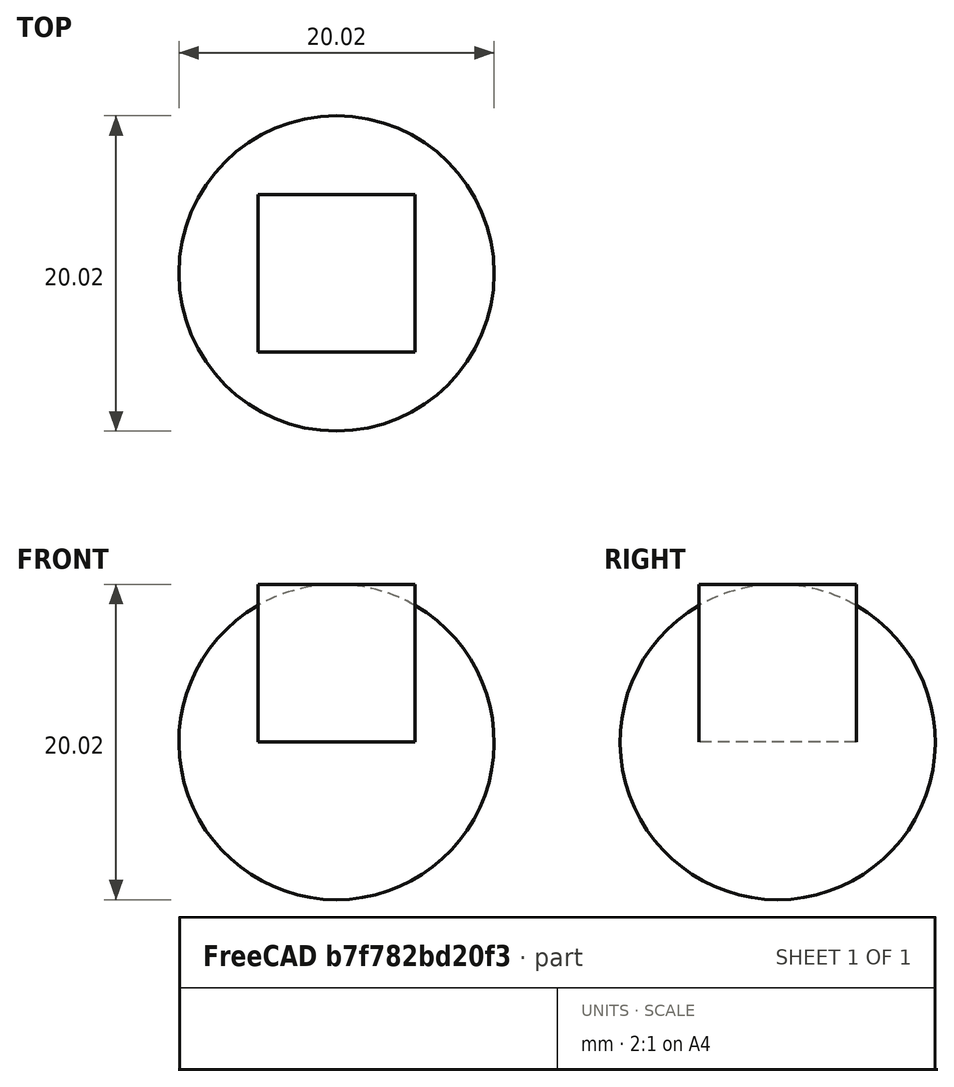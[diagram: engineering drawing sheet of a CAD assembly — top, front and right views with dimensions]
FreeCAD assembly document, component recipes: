
FREECAD ASSEMBLY — COMPONENT RECIPES ("test")

This assembly document has 2 components, labeled P0..P1 below (a component is one placed body or linked part). 2 of them carry a construction recipe — the FreeCAD feature program that regenerates the part from scratch, quoted from this document or its linked companion documents; the rest are supplied as boundary geometry only. No exploded tour is included for this assembly.
COMPONENT P0 — recipe-attached ("Cube", modeled in this document).
Construction recipe (the document's own serialized feature program — sketch geometry with constraints, then the solid features built on it; lengths are millimeters unless a unit is written):

FEATURE [PartDesign::CoordinateSystem] LCS_Origin001
  AttacherType = Attacher::AttachEngine3D
  MapMode = 2
  Support = -> [X_Axis001]
FEATURE [Sketcher::SketchObject] Sketch
  FullyConstrained = true
  MapMode = 5
  Support = -> [XY_Plane001]
  expr: Constraints[8] = Variables.size_cube
  sketch-geometry (4):
    g0: LineSegment StartX=-5 StartY=5 StartZ=0 EndX=5 EndY=5 EndZ=0
    g1: LineSegment StartX=5 StartY=5 StartZ=0 EndX=5 EndY=-5 EndZ=0
    g2: LineSegment StartX=5 StartY=-5 StartZ=0 EndX=-5 EndY=-5 EndZ=0
    g3: LineSegment StartX=-5 StartY=-5 StartZ=0 EndX=-5 EndY=5 EndZ=0
  constraints (10):
    c: Coincident(g0,g1)
    c: Coincident(g1,g2)
    c: Coincident(g2,g3)
    c: Coincident(g3,g0)
    c: Horizontal(g2)
    c: Vertical(g3)
    c: Symmetric(g0,g1,g-1)
    c: Symmetric(g0,g0,g-2)
    c: DistanceX(g0,g0) = 10
    c: Equal(g1,g0)
FEATURE [PartDesign::Pad] Pad
  Direction = (0,0,1)
  Length = 10
  Length2 = 10
  Profile = -> Sketch
  ReferenceAxis = -> Sketch [N_Axis]
  Type = 0
  expr: Length = Variables.size_cube
FEATURE [PartDesign::CoordinateSystem] MountSphere
  AttacherType = Attacher::AttachEngine3D
  MapMode = 5
  Placement = pos=(0,0,10) rot=(0,0,1;0rad)
  Support = -> [Pad]
FEATURE [PartDesign::Body] Cube
  Group = -> [LCS_Origin001,Sketch,Pad,MountSphere]
  Origin = -> Origin001
  Tip = -> Pad
COMPONENT P1 — recipe-attached ("Sphere", modeled in this document).
Construction recipe (the document's own serialized feature program — sketch geometry with constraints, then the solid features built on it; lengths are millimeters unless a unit is written):

FEATURE [PartDesign::CoordinateSystem] LCS_Origin002
  AttacherType = Attacher::AttachEngine3D
  MapMode = 2
  Support = -> [X_Axis002]
FEATURE [PartDesign::AdditiveSphere] Sphere001
  Angle1 = -90
  Angle2 = 90
  Angle3 = 360
  AttacherType = Attacher::AttachEngine3D
  Radius = 10.01
  expr: Radius = Variables.radius_sphere
FEATURE [PartDesign::CoordinateSystem] LCS_1
  AttacherType = Attacher::AttachEngine3D
  AttachmentOffset = pos=(0,0,-10.01) rot=(0,0,1;0rad)
  MapMode = 5
  Placement = pos=(0,0,-10.01) rot=(0,0,1;0rad)
  Support = -> [XY_Plane002]
  expr: .AttachmentOffset.Base.z = -Variables.radius_sphere
FEATURE [PartDesign::Body] Sphere
  Group = -> [LCS_Origin002,Sphere001,LCS_1]
  Origin = -> Origin002
  Tip = -> Sphere001
PROVENANCE & LICENSES
A FreeCAD (.FCStd) document from a public repository crawl; recipes are the document's own serialized feature recipes (and, for linked parts, companion documents' recipes).
License: as declared in the source repository (recorded in the dataset sidecar).
